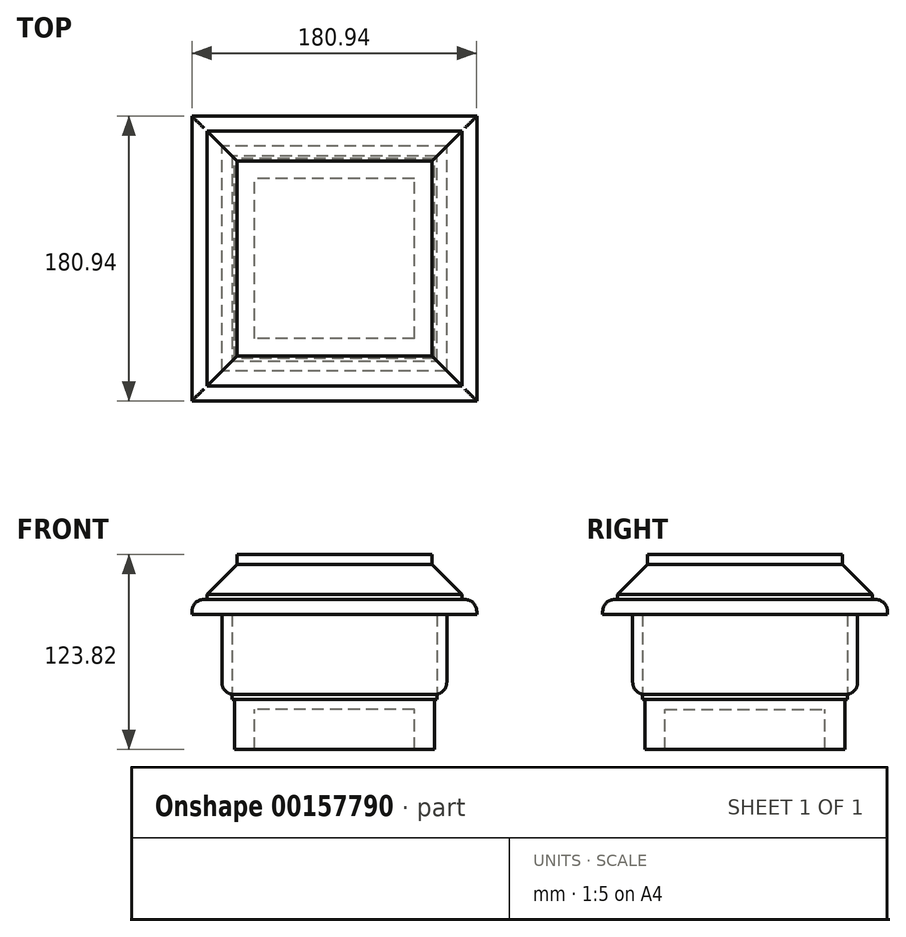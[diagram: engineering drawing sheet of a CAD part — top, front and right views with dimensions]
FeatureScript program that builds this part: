
annotation { "Feature Type Name" : "Feature", "Feature Type Description" : "" }
export const myFeature = defineFeature(function(context is Context, id is Id, definition is map)
    precondition{}
    {
        {
            var Q0;
            Q0=qCreatedBy(makeId("Top.planeOp"),FACE);
            var sketch = newSketch(context, id + "F0", { "sketchPlane" : qUnion([Q0])});
            skLineSegment(sketch, "E0.bottom", {"start": v(50.8, -50.8) * mm, "end": v(-50.8, -50.8) * mm});
            skLineSegment(sketch, "E0.top", {"start": v(50.8, 50.8) * mm, "end": v(-50.8, 50.8) * mm});
            skLineSegment(sketch, "E0.left", {"start": v(50.8, -50.8) * mm, "end": v(50.8, 50.8) * mm});
            skLineSegment(sketch, "E0.right", {"start": v(-50.8, -50.8) * mm, "end": v(-50.8, 50.8) * mm});
            skPoint(sketch, "E0.middle", {"position": v(0, 0) * mm});
            skLineSegment(sketch, "E1.0", {"start": v(-63.5, -63.5) * mm, "end": v(-63.5, 63.5) * mm});
            skLineSegment(sketch, "E1.1", {"start": v(63.5, -63.5) * mm, "end": v(-63.5, -63.5) * mm});
            skLineSegment(sketch, "E1.2", {"start": v(63.5, -63.5) * mm, "end": v(63.5, 63.5) * mm});
            skLineSegment(sketch, "E1.3", {"start": v(63.5, 63.5) * mm, "end": v(-63.5, 63.5) * mm});
            skSolve(sketch);
        }
        {
            var Q0;
            Q0 = qSketchRegion(id + "F0", true);
            extrude(context, id + "F1", {"entities" : qUnion([Q0]), "oppositeDirection" : true, "depth" : 25.4 * mm});
        }
        {
            var Q0;
            Q0=makeQuery(id+"F0.imprint","IMPRINT",FACE,{"disambiguationData":[TD([[makeQuery(id+"F0.imprint","IMPRINT",EDGE,{"derivedFrom":sQuery(id+"F0.wireOp",EDGE,"E0.bottom")}),1.0]])]});
            var Q1;
            Q1=makeQuery(id+"F0.imprint","IMPRINT",FACE,{"disambiguationData":[TD([[makeQuery(id+"F0.imprint","IMPRINT",EDGE,{"derivedFrom":sQuery(id+"F0.wireOp",EDGE,"E0.bottom")}),-1.0]])]});
            extrude(context, id + "F2", {"entities" : qUnion([Q0, Q1]), "operationType" : NewBodyOperationType.ADD, "depth" : 6.35 * mm});
        }
        {
            var Q0;
            Q0=makeQuery(id+"F2.opExtrude","CAP_FACE",FACE,{"disambiguationData":[OSD([sQuery(id+"F0.wireOp",EDGE,"E1.0"),sQuery(id+"F0.wireOp",EDGE,"E1.1"),sQuery(id+"F0.wireOp",EDGE,"E1.2"),sQuery(id+"F0.wireOp",EDGE,"E1.3")])],"isStart":false});
            var sketch = newSketch(context, id + "F3", { "sketchPlane" : qUnion([Q0])});
            skLineSegment(sketch, "E2.0", {"start": v(63.5, 63.5) * mm, "end": v(-63.5, 63.5) * mm});
            skLineSegment(sketch, "E3.0", {"start": v(63.5, -63.5) * mm, "end": v(63.5, 63.5) * mm});
            skLineSegment(sketch, "E4.0", {"start": v(-63.5, -63.5) * mm, "end": v(-63.5, 63.5) * mm});
            skLineSegment(sketch, "E5.0", {"start": v(63.5, -63.5) * mm, "end": v(-63.5, -63.5) * mm});
            skLineSegment(sketch, "E6.0", {"start": v(-65.07, -65.07) * mm, "end": v(-65.07, 65.07) * mm});
            skLineSegment(sketch, "E6.1", {"start": v(65.07, -65.07) * mm, "end": v(-65.07, -65.07) * mm});
            skLineSegment(sketch, "E6.2", {"start": v(65.07, -65.07) * mm, "end": v(65.07, 65.07) * mm});
            skLineSegment(sketch, "E6.3", {"start": v(65.07, 65.07) * mm, "end": v(-65.07, 65.07) * mm});
            skSolve(sketch);
        }
        {
            var Q0;
            Q0 = qSketchRegion(id + "F3", true);
            var Q1;
            Q1=makeQuery(id+"F3.imprint","IMPRINT",FACE,{"disambiguationData":[TD([[makeQuery(id+"F3.imprint","IMPRINT",EDGE,{"derivedFrom":sQuery(id+"F3.wireOp",EDGE,"E2.0")}),1.0]])]});
            extrude(context, id + "F4", {"entities" : qUnion([Q0, Q1]), "operationType" : NewBodyOperationType.ADD, "depth" : 3.17 * mm});
        }
        {
            var Q0;
            Q0=makeQuery(id+"F4.opExtrude","CAP_FACE",FACE,{"disambiguationData":[OSD([sQuery(id+"F3.wireOp",EDGE,"E6.0"),sQuery(id+"F3.wireOp",EDGE,"E6.1"),sQuery(id+"F3.wireOp",EDGE,"E6.2"),sQuery(id+"F3.wireOp",EDGE,"E6.3")])],"isStart":false});
            var sketch = newSketch(context, id + "F5", { "sketchPlane" : qUnion([Q0])});
            skLineSegment(sketch, "E7.0", {"start": v(65.07, 65.07) * mm, "end": v(-65.07, 65.07) * mm});
            skLineSegment(sketch, "E8.0", {"start": v(-65.07, -65.07) * mm, "end": v(-65.07, 65.07) * mm});
            skLineSegment(sketch, "E9.0", {"start": v(65.07, -65.07) * mm, "end": v(-65.07, -65.07) * mm});
            skLineSegment(sketch, "E10.0", {"start": v(65.07, -65.07) * mm, "end": v(65.07, 65.07) * mm});
            skLineSegment(sketch, "E11.0", {"start": v(71.42, 71.42) * mm, "end": v(-71.42, 71.42) * mm});
            skLineSegment(sketch, "E11.1", {"start": v(71.42, -71.42) * mm, "end": v(71.42, 71.42) * mm});
            skLineSegment(sketch, "E11.2", {"start": v(71.42, -71.42) * mm, "end": v(-71.42, -71.42) * mm});
            skLineSegment(sketch, "E11.3", {"start": v(-71.42, -71.42) * mm, "end": v(-71.42, 71.42) * mm});
            skSolve(sketch);
        }
        {
            var Q0;
            Q0 = qSketchRegion(id + "F5", true);
            extrude(context, id + "F6", {"entities" : qUnion([Q0]), "flatOperationType" : FlatOperationType.REMOVE, "offsetDistance" : 25.4 * mm, "depth" : 50.8 * mm, "domain" : OperationDomain.MODEL});
        }
        {
            var Q0;
            Q0=makeQuery(id+"F6.opExtrude","CAP_FACE",FACE,{"disambiguationData":[OSD([sQuery(id+"F5.wireOp",EDGE,"E7.0"),sQuery(id+"F5.wireOp",EDGE,"E8.0"),sQuery(id+"F5.wireOp",EDGE,"E9.0"),sQuery(id+"F5.wireOp",EDGE,"E10.0"),sQuery(id+"F5.wireOp",EDGE,"E11.0"),sQuery(id+"F5.wireOp",EDGE,"E11.1"),sQuery(id+"F5.wireOp",EDGE,"E11.2"),sQuery(id+"F5.wireOp",EDGE,"E11.3")])],"isStart":false});
            var sketch = newSketch(context, id + "F7", { "sketchPlane" : qUnion([Q0])});
            skLineSegment(sketch, "E12.0", {"start": v(71.42, 71.42) * mm, "end": v(-71.42, 71.42) * mm});
            skLineSegment(sketch, "E13.0", {"start": v(71.42, -71.42) * mm, "end": v(71.42, 71.42) * mm});
            skLineSegment(sketch, "E14.0", {"start": v(71.42, -71.42) * mm, "end": v(-71.42, -71.42) * mm});
            skLineSegment(sketch, "E15.0", {"start": v(-71.42, -71.42) * mm, "end": v(-71.42, 71.42) * mm});
            skLineSegment(sketch, "E16.0", {"start": v(90.47, -90.47) * mm, "end": v(-90.47, -90.47) * mm});
            skLineSegment(sketch, "E16.1", {"start": v(90.47, -90.47) * mm, "end": v(90.47, 90.47) * mm});
            skLineSegment(sketch, "E16.2", {"start": v(90.47, 90.47) * mm, "end": v(-90.47, 90.47) * mm});
            skLineSegment(sketch, "E16.3", {"start": v(-90.47, -90.47) * mm, "end": v(-90.47, 90.47) * mm});
            skSolve(sketch);
        }
        {
            var Q0;
            Q0=makeQuery(id+"F7.imprint","IMPRINT",FACE,{"disambiguationData":[TD([[makeQuery(id+"F7.imprint","IMPRINT",EDGE,{"derivedFrom":sQuery(id+"F7.wireOp",EDGE,"E12.0")}),-1.0]])]});
            var Q1;
            Q1=makeQuery(id+"F7.imprint","IMPRINT",FACE,{"disambiguationData":[TD([[makeQuery(id+"F7.imprint","IMPRINT",EDGE,{"derivedFrom":makeQuery(id+"F6.opExtrude","CAP_EDGE",EDGE,{"disambiguationData":[OSD([sQuery(id+"F5.wireOp",EDGE,"E7.0")])],"isStart":false})}),1.0]])]});
            var Q2;
            Q2=makeQuery(id+"F7.imprint","IMPRINT",FACE,{"disambiguationData":[TD([[makeQuery(id+"F7.imprint","IMPRINT",EDGE,{"derivedFrom":sQuery(id+"F7.wireOp",EDGE,"E12.0")}),1.0]])]});
            extrude(context, id + "F8", {"entities" : qUnion([Q0, Q1, Q2]), "flatOperationType" : FlatOperationType.REMOVE, "offsetDistance" : 25.4 * mm, "depth" : 9.52 * mm, "domain" : OperationDomain.MODEL});
        }
        {
            var Q0;
            Q0=makeQuery(id+"F8.opExtrude","CAP_FACE",FACE,{"disambiguationData":[OSD([sQuery(id+"F7.wireOp",EDGE,"E16.0"),sQuery(id+"F7.wireOp",EDGE,"E16.1"),sQuery(id+"F7.wireOp",EDGE,"E16.2"),sQuery(id+"F7.wireOp",EDGE,"E16.3")])],"isStart":false});
            var sketch = newSketch(context, id + "F9", { "sketchPlane" : qUnion([Q0])});
            skLineSegment(sketch, "E17.0", {"start": v(90.47, 90.47) * mm, "end": v(-90.47, 90.47) * mm});
            skLineSegment(sketch, "E18.0", {"start": v(-90.47, -90.47) * mm, "end": v(-90.47, 90.47) * mm});
            skLineSegment(sketch, "E19.0", {"start": v(90.47, -90.47) * mm, "end": v(-90.47, -90.47) * mm});
            skLineSegment(sketch, "E20.0", {"start": v(90.47, -90.47) * mm, "end": v(90.47, 90.47) * mm});
            skLineSegment(sketch, "E21.0", {"start": v(80.95, 80.95) * mm, "end": v(-80.95, 80.95) * mm});
            skLineSegment(sketch, "E21.1", {"start": v(80.95, -80.95) * mm, "end": v(80.95, 80.95) * mm});
            skLineSegment(sketch, "E21.2", {"start": v(80.95, -80.95) * mm, "end": v(-80.95, -80.95) * mm});
            skLineSegment(sketch, "E21.3", {"start": v(-80.95, -80.95) * mm, "end": v(-80.95, 80.95) * mm});
            skSolve(sketch);
        }
        {
            var Q0;
            Q0=makeQuery(id+"F9.imprint","IMPRINT",FACE,{"disambiguationData":[TD([[makeQuery(id+"F9.imprint","IMPRINT",EDGE,{"derivedFrom":sQuery(id+"F9.wireOp",EDGE,"E21.0")}),1.0]])]});
            extrude(context, id + "F10", {"entities" : qUnion([Q0]), "operationType" : NewBodyOperationType.ADD, "depth" : 3.17 * mm});
        }
        {
            var Q0;
            Q0=makeQuery(id+"F10.opExtrude","CAP_FACE",FACE,{"disambiguationData":[OSD([sQuery(id+"F9.wireOp",EDGE,"E21.0"),sQuery(id+"F9.wireOp",EDGE,"E21.1"),sQuery(id+"F9.wireOp",EDGE,"E21.2"),sQuery(id+"F9.wireOp",EDGE,"E21.3")])],"isStart":false});
            extrude(context, id + "F11", {"entities" : qUnion([Q0]), "operationType" : NewBodyOperationType.ADD, "depth" : 19.05 * mm, "hasDraft" : true, "draftAngle" : 45 * degree, "draftPullDirection" : true});
        }
        {
            var Q0;
            Q0=makeQuery(id+"F11.opExtrude","CAP_FACE",FACE,{"disambiguationData":[OSD([sQuery(id+"F9.wireOp",EDGE,"E21.0"),sQuery(id+"F9.wireOp",EDGE,"E21.1"),sQuery(id+"F9.wireOp",EDGE,"E21.2"),sQuery(id+"F9.wireOp",EDGE,"E21.3")])],"isStart":false});
            extrude(context, id + "F12", {"entities" : qUnion([Q0]), "operationType" : NewBodyOperationType.ADD, "depth" : 6.35 * mm});
        }
        {
            var Q0;
            Q0=makeQuery(id+"F6.opExtrude","CAP_EDGE",EDGE,{"disambiguationData":[OSD([sQuery(id+"F5.wireOp",EDGE,"E11.1")])],"isStart":true});
            var Q1;
            Q1=makeQuery(id+"F6.opExtrude","CAP_EDGE",EDGE,{"disambiguationData":[OSD([sQuery(id+"F5.wireOp",EDGE,"E11.0")])],"isStart":true});
            var Q2;
            Q2=makeQuery(id+"F6.opExtrude","CAP_EDGE",EDGE,{"disambiguationData":[OSD([sQuery(id+"F5.wireOp",EDGE,"E11.2")])],"isStart":true});
            var Q3;
            Q3=makeQuery(id+"F6.opExtrude","CAP_EDGE",EDGE,{"disambiguationData":[OSD([sQuery(id+"F5.wireOp",EDGE,"E11.3")])],"isStart":true});
            fillet(context, id + "F13", {"entities" : qUnion([Q0, Q1, Q2, Q3]), "radius" : 7.62 * mm, "tangentPropagation" : true, "allowEdgeOverflow" : false});
        }
        {
            var Q0;
            Q0=makeQuery(id+"F8.opExtrude","CAP_EDGE",EDGE,{"disambiguationData":[OSD([sQuery(id+"F7.wireOp",EDGE,"E16.1")])],"isStart":false});
            var Q1;
            Q1=makeQuery(id+"F8.opExtrude","CAP_EDGE",EDGE,{"disambiguationData":[OSD([sQuery(id+"F7.wireOp",EDGE,"E16.0")])],"isStart":false});
            var Q2;
            Q2=makeQuery(id+"F8.opExtrude","CAP_EDGE",EDGE,{"disambiguationData":[OSD([sQuery(id+"F7.wireOp",EDGE,"E16.3")])],"isStart":false});
            var Q3;
            Q3=makeQuery(id+"F8.opExtrude","CAP_EDGE",EDGE,{"disambiguationData":[OSD([sQuery(id+"F7.wireOp",EDGE,"E16.2")])],"isStart":false});
            fillet(context, id + "F14", {"entities" : qUnion([Q0, Q1, Q2, Q3]), "radius" : 7.62 * mm, "tangentPropagation" : true, "allowEdgeOverflow" : false});
        }
    });
